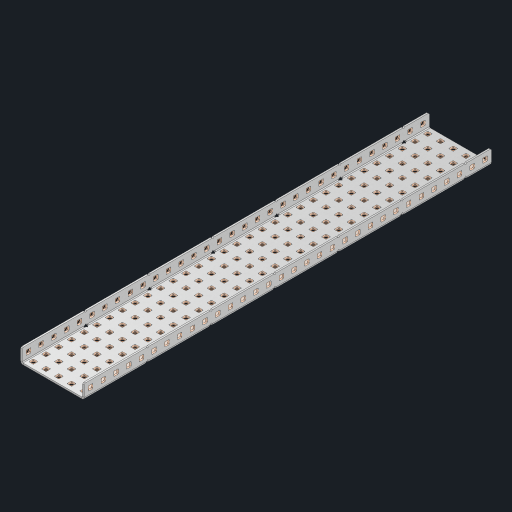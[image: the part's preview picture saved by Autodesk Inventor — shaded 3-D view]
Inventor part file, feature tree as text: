
AUTODESK INVENTOR PART (.ipt)
format: ipt  version: 2023 (Build 270158000, 158)  size: 2,361,856 bytes
history: native  units: in
note: dims shown in document units (in); Inventor stores cm internally (conversion verified against a paired STEP export)
features: other x229, extrude x223, sheet_metal_op x10, sketch x8, mirror x1, pattern_linear x1, chamfer x1
ambient origin geometry x8: Origin, YZ Plane, XZ Plane, XY Plane, X Axis, Y Axis, Z Axis, Center Point
bodies: Solid1 (feature_tree), Body (feature_tree)
feature tree (473):
  other  "Flange Pattern Plane"
  sheet_metal_op  "Flange Pattern"
  sheet_metal_op  "Body Pattern"
  other  "Arc Length"
  mirror  "Notch Mirror"
  pattern_linear  "Notch Pattern"  Spacing1=0.25in  [1 undecoded]
  chamfer  "End Chamfer"
  extrude  "Half Cut"  Depth=0.0625in
  sketch  "Sketch1"  dims[d0=2.5in]
  other  "Plate1"
  sketch  "Sketch2"  dims[d1=16.0in]
  other  "Plate2"
  sheet_metal_op  "Bend1"
  sheet_metal_op  "Corner1"
  sketch  "Sketch3"  dims[d2=0.0625in]
  other  "Flange Pattern Sketch"
  sketch  "Sketch7"  dims[d3=0.0625in]
  other  "Srf1"
  other  "Srf2"
  sketch  "Sketch8"  dims[d4=0.0312in]
  sketch  "Sketch9"  dims[d5=0.125in]
  other  "Srf91"
  sheet_metal_op  "Body Pattern Sketch"
  other  "Srf92"
  sketch  "Sketch13"  dims[d6=0.0625in]
  sketch  "Sketch14"  dims[d7=0.5in d8=90.0deg d9=0.0312in d10=0.25in d11=0.0625in d12=0.0625in d16=0.182in d17=0.02in d18=0.0625in d19=0.0in d20=0.25in d21=0.25in d46=0.172in d47=1.0in d48=0.0in d49=0.182in d50=0.02in d51=0.25in d52=0.25in d53=0.0625in d54=0.0in d55=0.172in d56=1.0in d57=0.0in d60=12.5984in d62=0.5in d63=1.9685in d65=0.5in d85=0.1473in d86=0.1782in d88=0.04in d89=0.0625in d90=0.0in d91=0.04in d92=0.0491in d95=2.5in d96=0.04in d97=0.25in d98=45.0deg d101=0.0in d102=2.497in d131=2.5in d132=12.5984in d134=0.5in d139=0.5in]
  other  "Srf856"
  other  "Srf1310"
  other  "Srf1311"
  other  "Srf1312"
  other  "Srf1376"
  other  "Srf1377"
  other  "Srf1728"
  other  "Srf1755"
  other  "Srf1878"
  other  "Srf1879"
  other  "Srf1880"
  other  "Srf1881"
  other  "Srf1882"
  other  "Srf1883"
  other  "Srf1884"
  other  "Srf1885"
  other  "Srf1886"
  other  "Srf1887"
  other  "Srf1888"
  other  "Srf1889"
  other  "Srf1890"
  other  "Srf1891"
  other  "Srf1892"
  other  "Srf1893"
  other  "Srf1894"
  other  "Srf1895"
  other  "Srf1896"
  other  "Srf1897"
  other  "Srf1898"
  other  "Srf1899"
  other  "Srf1900"
  other  "Srf1901"
  other  "Srf1902"
  other  "Srf1903"
  other  "Srf1904"
  other  "Srf1905"
  other  "Srf1906"
  other  "Srf1942"
  other  "Srf1943"
  other  "Srf1944"
  other  "Srf1945"
  other  "Srf1946"
  other  "Srf1947"
  other  "Srf1948"
  other  "Srf1949"
  other  "Srf1950"
  other  "Srf1951"
  other  "Srf1952"
  other  "Srf1953"
  other  "Srf1954"
  other  "Srf1955"
  other  "Srf1956"
  other  "Srf1957"
  other  "Srf1958"
  other  "Srf1959"
  other  "Srf1960"
  other  "Srf1961"
  other  "Srf1962"
  other  "Srf1963"
  other  "Srf1964"
  other  "Srf1965"
  other  "Srf1966"
  other  "Srf1967"
  other  "Srf1968"
  other  "Srf1969"
  other  "Srf1970"
  other  "Srf2111"
  other  "Srf2112"
  other  "Srf2113"
  other  "Srf2114"
  other  "Srf2115"
  other  "Srf2116"
  other  "Srf2117"
  other  "Srf2118"
  other  "Srf2119"
  other  "Srf2120"
  other  "Srf2121"
  other  "Srf2122"
  other  "Srf2123"
  other  "Srf2124"
  other  "Srf2125"
  other  "Srf2126"
  other  "Srf2127"
  other  "Srf2128"
  other  "Srf2129"
  other  "Srf2130"
  other  "Srf2131"
  other  "Srf2132"
  other  "Srf2133"
  other  "Srf2134"
  other  "Srf2135"
  other  "Srf2136"
  other  "Srf2137"
  other  "Srf2138"
  other  "Srf2139"
  other  "Srf2146"
  other  "Srf2147"
  other  "Srf2148"
  other  "Srf2149"
  other  "Srf2150"
  other  "Srf2151"
  other  "Srf2152"
  other  "Srf2153"
  other  "Srf2154"
  other  "Srf2155"
  other  "Srf2156"
  other  "Srf2157"
  other  "Srf2158"
  other  "Srf2159"
  other  "Srf2160"
  other  "Srf2161"
  other  "Srf2162"
  other  "Srf2163"
  other  "Srf2164"
  other  "Srf2165"
  other  "Srf2166"
  other  "Srf2167"
  other  "Srf2168"
  other  "Srf2169"
  other  "Srf2170"
  other  "Srf2171"
  other  "Srf2172"
  other  "Srf2173"
  other  "Srf2174"
  other  "Srf2175"
  other  "Srf2176"
  other  "Srf2177"
  other  "Srf2178"
  other  "Srf2179"
  other  "Srf2180"
  other  "Srf2181"
  other  "Srf2182"
  other  "Srf2183"
  other  "Srf2184"
  other  "Srf2185"
  other  "Srf2186"
  other  "Srf2187"
  other  "Srf2188"
  other  "Srf2189"
  other  "Srf2190"
  other  "Srf2191"
  other  "Srf2192"
  other  "Srf2193"
  other  "Srf2194"
  other  "Srf2195"
  other  "Srf2196"
  other  "Srf2197"
  other  "Srf2198"
  other  "Srf2199"
  other  "Srf2200"
  other  "Srf2201"
  other  "Srf2202"
  other  "Srf2203"
  other  "Srf2204"
  other  "Srf2205"
  other  "Srf2206"
  other  "Srf2207"
  other  "Srf2208"
  other  "Srf2209"
  other  "Srf2210"
  other  "Srf2211"
  other  "Srf2212"
  other  "Srf2213"
  other  "Srf2214"
  other  "Srf2215"
  other  "Srf2216"
  other  "Srf2217"
  other  "Srf2218"
  other  "Srf2219"
  other  "Srf2220"
  other  "Srf2221"
  other  "Srf2222"
  other  "Srf2223"
  other  "Srf2224"
  other  "Srf2225"
  other  "Srf2226"
  other  "Srf2227"
  other  "Srf2228"
  other  "Srf2229"
  other  "Srf2230"
  other  "Srf2231"
  other  "Srf2232"
  other  "Srf2233"
  other  "Srf2234"
  other  "Srf2235"
  other  "Srf2236"
  other  "Srf2237"
  other  "Srf2238"
  other  "Srf2239"
  other  "Srf2240"
  other  "Srf2241"
  other  "Srf2242"
  other  "Srf2243"
  other  "Srf2244"
  other  "Srf2245"
  other  "Srf2246"
  other  "Srf2247"
  other  "Srf2248"
  other  "Srf2249"
  other  "Srf2250"
  other  "Srf2251"
  other  "Srf2252"
  other  "Srf2253"
  other  "Srf2254"
  other  "Srf2255"
  other  "Srf2256"
  other  "Srf2257"
  other  "Srf2258"
  other  "Srf2259"
  other  "Srf2260"
  other  "Srf2261"
  other  "Srf2262"
  other  "Srf2263"
  other  "Srf2264"
  other  "Srf2265"
  other  "Srf2266"
  other  "Srf2267"
  other  "Srf2268"
  other  "Srf2269"
  other  "Srf2270"
  sheet_metal_op  "Flange Stamp"
  sheet_metal_op  "Flange Circle"
  sheet_metal_op  "Body Stamp"
  sheet_metal_op  "Body Circle"
  sheet_metal_op  "Notch"
  extrude  "ExtrusionSrf2"  Depth=0.0625in
  extrude  "ExtrusionSrf92"  Depth=2.5in
  extrude  "ExtrusionSrf856"  Depth=0.02in
  extrude  "ExtrusionSrf1310"  Depth=0.0625in
  extrude  "ExtrusionSrf1311"  TaperAngle=0.0deg  [1 undecoded]
  extrude  "ExtrusionSrf1312"  Depth=0.25in
  extrude  "ExtrusionSrf1376"  Depth=0.25in
  extrude  "ExtrusionSrf1377"  Depth=2.5in
  extrude  "ExtrusionSrf1728"  Depth=2.5in TaperAngle=0.0deg
  extrude  "ExtrusionSrf1755"  Depth=2.5in
  extrude  "ExtrusionSrf1878"  Depth=0.02in
  extrude  "ExtrusionSrf1879"  Depth=0.25in
  extrude  "ExtrusionSrf1880"  Depth=0.25in
  extrude  "ExtrusionSrf1881"  Depth=0.0625in
  extrude  "ExtrusionSrf1882"  TaperAngle=0.0deg  [1 undecoded]
  extrude  "ExtrusionSrf1883"  Depth=2.5in
  extrude  "ExtrusionSrf1884"  Depth=2.5in TaperAngle=0.0deg
  extrude  "ExtrusionSrf1885"  Depth=2.5in
  extrude  "ExtrusionSrf1886"  Depth=2.5in
  extrude  "ExtrusionSrf1887"  Depth=2.5in
  extrude  "ExtrusionSrf1888"  Depth=2.5in
  extrude  "ExtrusionSrf1889"  Depth=2.5in
  extrude  "ExtrusionSrf1890"  Depth=0.0625in
  extrude  "ExtrusionSrf1891"  TaperAngle=0.0deg  [1 undecoded]
  extrude  "ExtrusionSrf1892"  Depth=2.5in
  extrude  "ExtrusionSrf1893"  Depth=2.5in
  extrude  "ExtrusionSrf1894"  Depth=2.5in
  extrude  "ExtrusionSrf1895"  Depth=0.25in TaperAngle=45.0deg
  extrude  "ExtrusionSrf1896"  TaperAngle=0.0deg  [1 undecoded]
  extrude  "ExtrusionSrf1897"  Depth=2.5in
  extrude  "ExtrusionSrf1898"  Depth=2.5in
  extrude  "ExtrusionSrf1899"  Depth=2.5in
  extrude  "ExtrusionSrf1900"  Depth=2.5in
  extrude  "ExtrusionSrf1901"  Depth=2.5in
  extrude  "ExtrusionSrf1902"  [1 undecoded]
  extrude  "ExtrusionSrf1903"  [1 undecoded]
  extrude  "ExtrusionSrf1904"  [1 undecoded]
  extrude  "ExtrusionSrf1905"  [1 undecoded]
  extrude  "ExtrusionSrf1906"  [1 undecoded]
  extrude  "ExtrusionSrf1942"  [1 undecoded]
  extrude  "ExtrusionSrf1943"  [1 undecoded]
  extrude  "ExtrusionSrf1944"  [1 undecoded]
  extrude  "ExtrusionSrf1945"  [1 undecoded]
  extrude  "ExtrusionSrf1946"  [1 undecoded]
  extrude  "ExtrusionSrf1947"  [1 undecoded]
  extrude  "ExtrusionSrf1948"  [1 undecoded]
  extrude  "ExtrusionSrf1949"  [1 undecoded]
  extrude  "ExtrusionSrf1950"  [1 undecoded]
  extrude  "ExtrusionSrf1951"  [1 undecoded]
  extrude  "ExtrusionSrf1952"  [1 undecoded]
  extrude  "ExtrusionSrf1953"  [1 undecoded]
  extrude  "ExtrusionSrf1954"  [1 undecoded]
  extrude  "ExtrusionSrf1955"  [1 undecoded]
  extrude  "ExtrusionSrf1956"  [1 undecoded]
  extrude  "ExtrusionSrf1957"  [1 undecoded]
  extrude  "ExtrusionSrf1958"  [1 undecoded]
  extrude  "ExtrusionSrf1959"  [1 undecoded]
  extrude  "ExtrusionSrf1960"  [1 undecoded]
  extrude  "ExtrusionSrf1961"  [1 undecoded]
  extrude  "ExtrusionSrf1962"  [1 undecoded]
  extrude  "ExtrusionSrf1963"  [1 undecoded]
  extrude  "ExtrusionSrf1964"  [1 undecoded]
  extrude  "ExtrusionSrf1965"  [1 undecoded]
  extrude  "ExtrusionSrf1966"  [1 undecoded]
  extrude  "ExtrusionSrf1967"  [1 undecoded]
  extrude  "ExtrusionSrf1968"  [1 undecoded]
  extrude  "ExtrusionSrf1969"  [1 undecoded]
  extrude  "ExtrusionSrf1970"  [1 undecoded]
  extrude  "ExtrusionSrf2111"  [1 undecoded]
  extrude  "ExtrusionSrf2112"  [1 undecoded]
  extrude  "ExtrusionSrf2113"  [1 undecoded]
  extrude  "ExtrusionSrf2114"  [1 undecoded]
  extrude  "ExtrusionSrf2115"  [1 undecoded]
  extrude  "ExtrusionSrf2116"  [1 undecoded]
  extrude  "ExtrusionSrf2117"  [1 undecoded]
  extrude  "ExtrusionSrf2118"  [1 undecoded]
  extrude  "ExtrusionSrf2119"  [1 undecoded]
  extrude  "ExtrusionSrf2120"  [1 undecoded]
  extrude  "ExtrusionSrf2121"  [1 undecoded]
  extrude  "ExtrusionSrf2122"  [1 undecoded]
  extrude  "ExtrusionSrf2123"  [1 undecoded]
  extrude  "ExtrusionSrf2124"  [1 undecoded]
  extrude  "ExtrusionSrf2125"  [1 undecoded]
  extrude  "ExtrusionSrf2126"  [1 undecoded]
  extrude  "ExtrusionSrf2127"  [1 undecoded]
  extrude  "ExtrusionSrf2128"  [1 undecoded]
  extrude  "ExtrusionSrf2129"  [1 undecoded]
  extrude  "ExtrusionSrf2130"  [1 undecoded]
  extrude  "ExtrusionSrf2131"  [1 undecoded]
  extrude  "ExtrusionSrf2132"  [1 undecoded]
  extrude  "ExtrusionSrf2133"  [1 undecoded]
  extrude  "ExtrusionSrf2134"  [1 undecoded]
  extrude  "ExtrusionSrf2135"  [1 undecoded]
  extrude  "ExtrusionSrf2136"  [1 undecoded]
  extrude  "ExtrusionSrf2137"  [1 undecoded]
  extrude  "ExtrusionSrf2138"  [1 undecoded]
  extrude  "ExtrusionSrf2139"  [1 undecoded]
  extrude  "ExtrusionSrf2146"  [1 undecoded]
  extrude  "ExtrusionSrf2147"  [1 undecoded]
  extrude  "ExtrusionSrf2148"  [1 undecoded]
  extrude  "ExtrusionSrf2149"  [1 undecoded]
  extrude  "ExtrusionSrf2150"  [1 undecoded]
  extrude  "ExtrusionSrf2151"  [1 undecoded]
  extrude  "ExtrusionSrf2152"  [1 undecoded]
  extrude  "ExtrusionSrf2153"  [1 undecoded]
  extrude  "ExtrusionSrf2154"  [1 undecoded]
  extrude  "ExtrusionSrf2155"  [1 undecoded]
  extrude  "ExtrusionSrf2156"  [1 undecoded]
  extrude  "ExtrusionSrf2157"  [1 undecoded]
  extrude  "ExtrusionSrf2158"  [1 undecoded]
  extrude  "ExtrusionSrf2159"  [1 undecoded]
  extrude  "ExtrusionSrf2160"  [1 undecoded]
  extrude  "ExtrusionSrf2161"  [1 undecoded]
  extrude  "ExtrusionSrf2162"  [1 undecoded]
  extrude  "ExtrusionSrf2163"  [1 undecoded]
  extrude  "ExtrusionSrf2164"  [1 undecoded]
  extrude  "ExtrusionSrf2165"  [1 undecoded]
  extrude  "ExtrusionSrf2166"  [1 undecoded]
  extrude  "ExtrusionSrf2167"  [1 undecoded]
  extrude  "ExtrusionSrf2168"  [1 undecoded]
  extrude  "ExtrusionSrf2169"  [1 undecoded]
  extrude  "ExtrusionSrf2170"  [1 undecoded]
  extrude  "ExtrusionSrf2171"  [1 undecoded]
  extrude  "ExtrusionSrf2172"  [1 undecoded]
  extrude  "ExtrusionSrf2173"  [1 undecoded]
  extrude  "ExtrusionSrf2174"  [1 undecoded]
  extrude  "ExtrusionSrf2175"  [1 undecoded]
  extrude  "ExtrusionSrf2176"  [1 undecoded]
  extrude  "ExtrusionSrf2177"  [1 undecoded]
  extrude  "ExtrusionSrf2178"  [1 undecoded]
  extrude  "ExtrusionSrf2179"  [1 undecoded]
  extrude  "ExtrusionSrf2180"  [1 undecoded]
  extrude  "ExtrusionSrf2181"  [1 undecoded]
  extrude  "ExtrusionSrf2182"  [1 undecoded]
  extrude  "ExtrusionSrf2183"  [1 undecoded]
  extrude  "ExtrusionSrf2184"  [1 undecoded]
  extrude  "ExtrusionSrf2185"  [1 undecoded]
  extrude  "ExtrusionSrf2186"  [1 undecoded]
  extrude  "ExtrusionSrf2187"  [1 undecoded]
  extrude  "ExtrusionSrf2188"  [1 undecoded]
  extrude  "ExtrusionSrf2189"  [1 undecoded]
  extrude  "ExtrusionSrf2190"  [1 undecoded]
  extrude  "ExtrusionSrf2191"  [1 undecoded]
  extrude  "ExtrusionSrf2192"  [1 undecoded]
  extrude  "ExtrusionSrf2193"  [1 undecoded]
  extrude  "ExtrusionSrf2194"  [1 undecoded]
  extrude  "ExtrusionSrf2195"  [1 undecoded]
  extrude  "ExtrusionSrf2196"  [1 undecoded]
  extrude  "ExtrusionSrf2197"  [1 undecoded]
  extrude  "ExtrusionSrf2198"  [1 undecoded]
  extrude  "ExtrusionSrf2199"  [1 undecoded]
  extrude  "ExtrusionSrf2200"  [1 undecoded]
  extrude  "ExtrusionSrf2201"  [1 undecoded]
  extrude  "ExtrusionSrf2202"  [1 undecoded]
  extrude  "ExtrusionSrf2203"  [1 undecoded]
  extrude  "ExtrusionSrf2204"  [1 undecoded]
  extrude  "ExtrusionSrf2205"  [1 undecoded]
  extrude  "ExtrusionSrf2206"  [1 undecoded]
  extrude  "ExtrusionSrf2207"  [1 undecoded]
  extrude  "ExtrusionSrf2208"  [1 undecoded]
  extrude  "ExtrusionSrf2209"  [1 undecoded]
  extrude  "ExtrusionSrf2210"  [1 undecoded]
  extrude  "ExtrusionSrf2211"  [1 undecoded]
  extrude  "ExtrusionSrf2212"  [1 undecoded]
  extrude  "ExtrusionSrf2213"  [1 undecoded]
  extrude  "ExtrusionSrf2214"  [1 undecoded]
  extrude  "ExtrusionSrf2215"  [1 undecoded]
  extrude  "ExtrusionSrf2216"  [1 undecoded]
  extrude  "ExtrusionSrf2217"  [1 undecoded]
  extrude  "ExtrusionSrf2218"  [1 undecoded]
  extrude  "ExtrusionSrf2219"  [1 undecoded]
  extrude  "ExtrusionSrf2220"  [1 undecoded]
  extrude  "ExtrusionSrf2221"  [1 undecoded]
  extrude  "ExtrusionSrf2222"  [1 undecoded]
  extrude  "ExtrusionSrf2223"  [1 undecoded]
  extrude  "ExtrusionSrf2224"  [1 undecoded]
  extrude  "ExtrusionSrf2225"  [1 undecoded]
  extrude  "ExtrusionSrf2226"  [1 undecoded]
  extrude  "ExtrusionSrf2227"  [1 undecoded]
  extrude  "ExtrusionSrf2228"  [1 undecoded]
  extrude  "ExtrusionSrf2229"  [1 undecoded]
  extrude  "ExtrusionSrf2230"  [1 undecoded]
  extrude  "ExtrusionSrf2231"  [1 undecoded]
  extrude  "ExtrusionSrf2232"  [1 undecoded]
  extrude  "ExtrusionSrf2233"  [1 undecoded]
  extrude  "ExtrusionSrf2234"  [1 undecoded]
  extrude  "ExtrusionSrf2235"  [1 undecoded]
  extrude  "ExtrusionSrf2236"  [1 undecoded]
  extrude  "ExtrusionSrf2237"  [1 undecoded]
  extrude  "ExtrusionSrf2238"  [1 undecoded]
  extrude  "ExtrusionSrf2239"  [1 undecoded]
  extrude  "ExtrusionSrf2240"  [1 undecoded]
  extrude  "ExtrusionSrf2241"  [1 undecoded]
  extrude  "ExtrusionSrf2242"  [1 undecoded]
  extrude  "ExtrusionSrf2243"  [1 undecoded]
  extrude  "ExtrusionSrf2244"  [1 undecoded]
  extrude  "ExtrusionSrf2245"  [1 undecoded]
  extrude  "ExtrusionSrf2246"  [1 undecoded]
  extrude  "ExtrusionSrf2247"  [1 undecoded]
  extrude  "ExtrusionSrf2248"  [1 undecoded]
  extrude  "ExtrusionSrf2249"  [1 undecoded]
  extrude  "ExtrusionSrf2250"  [1 undecoded]
  extrude  "ExtrusionSrf2251"  [1 undecoded]
  extrude  "ExtrusionSrf2252"  [1 undecoded]
  extrude  "ExtrusionSrf2253"  [1 undecoded]
  extrude  "ExtrusionSrf2254"  [1 undecoded]
  extrude  "ExtrusionSrf2255"  [1 undecoded]
  extrude  "ExtrusionSrf2256"  [1 undecoded]
  extrude  "ExtrusionSrf2257"  [1 undecoded]
  extrude  "ExtrusionSrf2258"  [1 undecoded]
  extrude  "ExtrusionSrf2259"  [1 undecoded]
  extrude  "ExtrusionSrf2260"  [1 undecoded]
  extrude  "ExtrusionSrf2261"  [1 undecoded]
  extrude  "ExtrusionSrf2262"  [1 undecoded]
  extrude  "ExtrusionSrf2263"  [1 undecoded]
  extrude  "ExtrusionSrf2264"  [1 undecoded]
  extrude  "ExtrusionSrf2265"  [1 undecoded]
  extrude  "ExtrusionSrf2266"  [1 undecoded]
  extrude  "ExtrusionSrf2267"  [1 undecoded]
  extrude  "ExtrusionSrf2268"  [1 undecoded]
  extrude  "ExtrusionSrf2269"  [1 undecoded]
  extrude  "ExtrusionSrf2270"  [1 undecoded]
note: 193 required parameter values undecoded (feature->parameter linkage not recoverable at this tier; creation-order binding heuristic only, values carry confidence <= 0.55)
